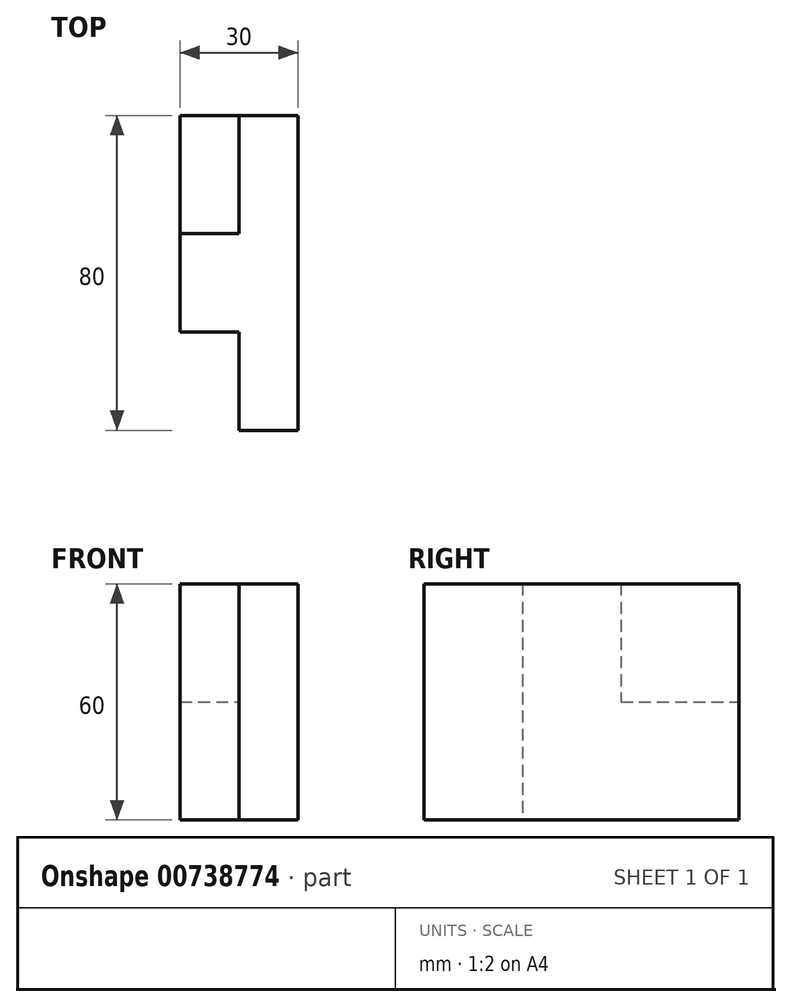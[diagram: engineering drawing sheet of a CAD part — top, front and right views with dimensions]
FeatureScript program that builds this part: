
annotation { "Feature Type Name" : "Feature", "Feature Type Description" : "" }
export const myFeature = defineFeature(function(context is Context, id is Id, definition is map)
    precondition{}
    {
        {
            var Q0;
            Q0=qCreatedBy(makeId("Top.planeOp"),FACE);
            var sketch = newSketch(context, id + "F0", { "sketchPlane" : qUnion([Q0])});
            skLineSegment(sketch, "E0", {"start": v(-30, 0) * mm, "end": v(0, 0) * mm});
            skLineSegment(sketch, "E1", {"start": v(0, 0) * mm, "end": v(0, -80) * mm});
            skLineSegment(sketch, "E2", {"start": v(0, -80) * mm, "end": v(-15, -80) * mm});
            skLineSegment(sketch, "E3", {"start": v(-15, -80) * mm, "end": v(-15, -55) * mm});
            skLineSegment(sketch, "E4", {"start": v(-15, -55) * mm, "end": v(-30, -55) * mm});
            skLineSegment(sketch, "E5", {"start": v(-30, -55) * mm, "end": v(-30, 0) * mm});
            skLineSegment(sketch, "E6", {"start": v(-30, -30) * mm, "end": v(-15, -30) * mm});
            skLineSegment(sketch, "E7", {"start": v(-15, -30) * mm, "end": v(-15, 0) * mm});
            skSolve(sketch);
        }
        {
            var Q0;
            {var subQ0=sQuery(id+"F0.wireOp",EDGE,"E1");Q0=makeQuery(id+"F0.imprint","IMPRINT",FACE,{"disambiguationData":[TD([[makeQuery(id+"F0.imprint","IMPRINT",EDGE,{"derivedFrom":subQ0}),-1.0]])]});}
            extrude(context, id + "F1", {"entities" : qUnion([Q0]), "depth" : 60 * mm, "offsetDistance" : 25 * mm});
        }
        {
            var Q0;
            {var subQ4=sQuery(id+"F0.wireOp",EDGE,"E6");Q0=makeQuery(id+"F0.imprint","IMPRINT",FACE,{"disambiguationData":[TD([[makeQuery(id+"F0.imprint","IMPRINT",EDGE,{"derivedFrom":subQ4}),1.0]])]});}
            extrude(context, id + "F2", {"entities" : qUnion([Q0]), "operationType" : NewBodyOperationType.ADD, "depth" : 30 * mm, "offsetDistance" : 25 * mm});
        }
    });
